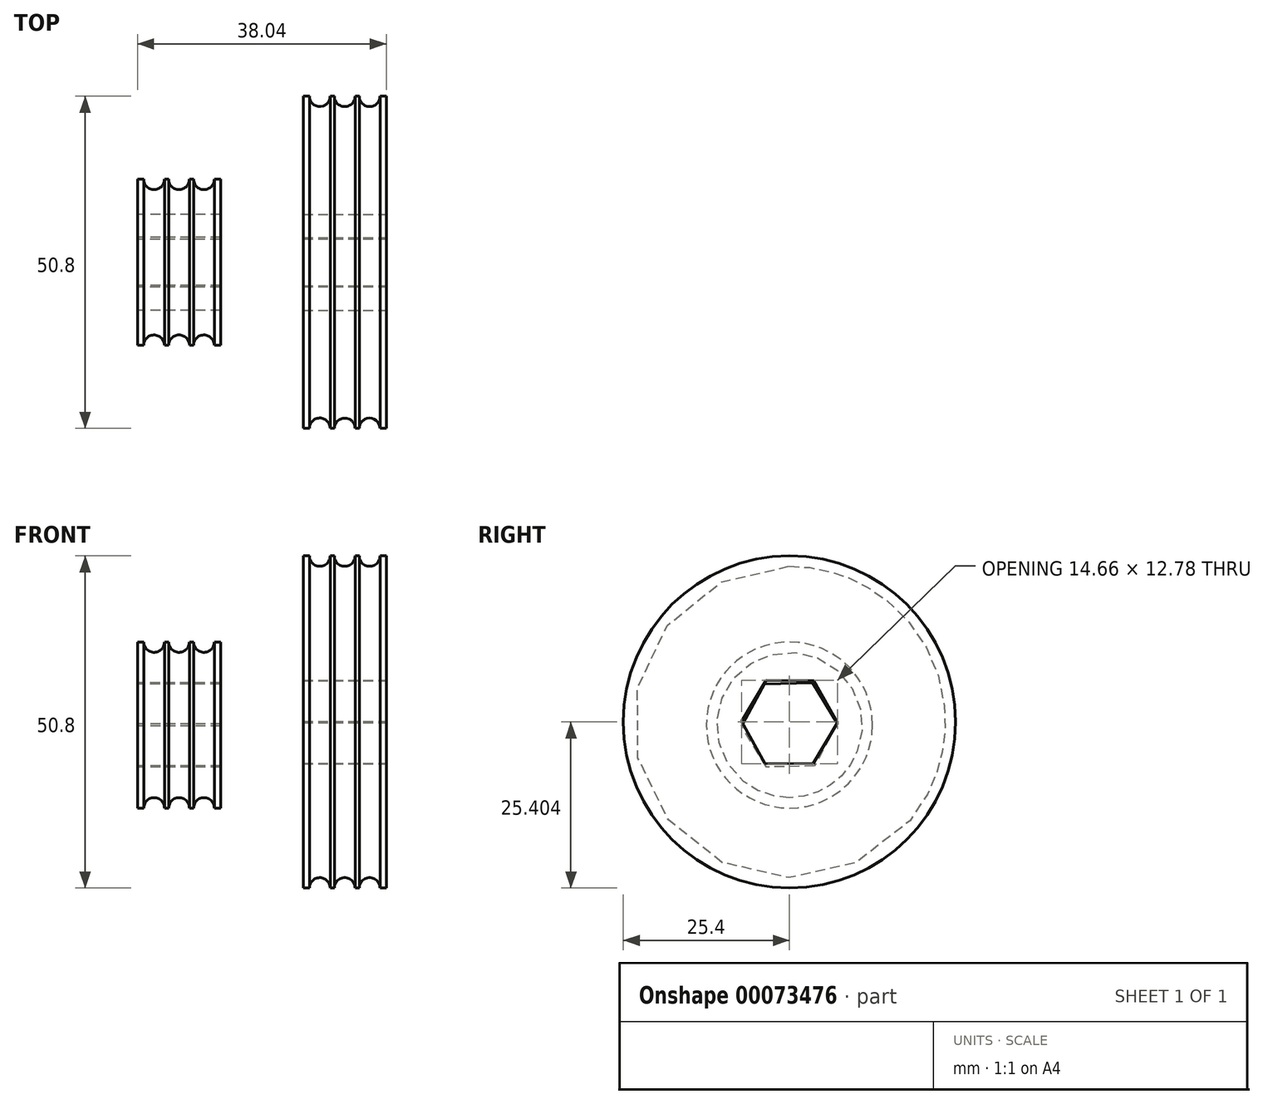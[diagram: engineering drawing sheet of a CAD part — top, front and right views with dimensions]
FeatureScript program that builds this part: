
annotation { "Feature Type Name" : "Feature", "Feature Type Description" : "" }
export const myFeature = defineFeature(function(context is Context, id is Id, definition is map)
    precondition{}
    {
        {
            var Q0;
            Q0=qCreatedBy(makeId("Front.planeOp"),FACE);
            var sketch = newSketch(context, id + "F0", { "sketchPlane" : qUnion([Q0])});
            skArc(sketch, "E0", {"start": v(1.58, 24.65) * mm, "mid": v(3.17, 23.06) * mm, "end": v(4.76, 24.65) * mm});
            skArc(sketch, "E1", {"start": v(5.4, 24.65) * mm, "mid": v(6.98, 23.06) * mm, "end": v(8.57, 24.65) * mm});
            skArc(sketch, "E2", {"start": v(9.2, 24.65) * mm, "mid": v(10.8, 23.06) * mm, "end": v(12.38, 24.65) * mm});
            skLineSegment(sketch, "E3", {"start": v(0.63, 24.65) * mm, "end": v(1.58, 24.65) * mm});
            skLineSegment(sketch, "E4", {"start": v(0.63, 11.95) * mm, "end": v(0.63, 24.65) * mm});
            skLineSegment(sketch, "E5", {"start": v(13.33, 24.65) * mm, "end": v(13.33, 11.95) * mm});
            skLineSegment(sketch, "E6.trimOffspring", {"start": v(4.76, 24.65) * mm, "end": v(5.4, 24.65) * mm});
            skLineSegment(sketch, "E7.trimOffspring", {"start": v(8.57, 24.65) * mm, "end": v(9.2, 24.65) * mm});
            skLineSegment(sketch, "E8.trimOffspring", {"start": v(12.38, 24.65) * mm, "end": v(13.33, 24.65) * mm});
            skPoint(sketch, "E9.start.orphan", {"position": v(-0.82, 11.95) * mm});
            skLineSegment(sketch, "E10", {"start": v(13.33, 11.95) * mm, "end": v(0.63, 11.95) * mm});
            skSolve(sketch);
        }
        {
            var Q0;
            Q0=makeQuery(id+"F0.imprint","IMPRINT",FACE,{"disambiguationData":[TD([[makeQuery(id+"F0.imprint","IMPRINT",EDGE,{"derivedFrom":sQuery(id+"F0.wireOp",EDGE,"E0")}),-1.0]])]});
            var Q1;
            Q1=sQuery(id+"F0.wireOp",EDGE,"E10");
            revolve(context, id + "F1", {"entities" : qUnion([Q0]), "axis" : qUnion([Q1]), "revolveType" : RevolveType.FULL});
        }
        {
            var Q0;
            Q0=qCreatedBy(makeId("Right.planeOp"),FACE);
            var sketch = newSketch(context, id + "F2", { "sketchPlane" : qUnion([Q0])});
            skCircle(sketch, "E11.cCircle", {"center": v(0, 11.95) * mm, "radius": 6.35 * mm, "construction": true});
            skLineSegment(sketch, "E11.0", {"start": v(7.33, 12.12) * mm, "end": v(3.81, 5.69) * mm});
            skLineSegment(sketch, "E11.1", {"start": v(3.81, 5.69) * mm, "end": v(-3.52, 5.52) * mm});
            skLineSegment(sketch, "E11.2", {"start": v(-3.52, 5.52) * mm, "end": v(-7.33, 11.78) * mm});
            skLineSegment(sketch, "E11.3", {"start": v(-7.33, 11.78) * mm, "end": v(-3.81, 18.21) * mm});
            skLineSegment(sketch, "E11.4", {"start": v(-3.81, 18.21) * mm, "end": v(3.52, 18.38) * mm});
            skLineSegment(sketch, "E11.5", {"start": v(3.52, 18.38) * mm, "end": v(7.33, 12.12) * mm});
            skPoint(sketch, "E11.0.midPoint", {"position": v(5.57, 8.9) * mm});
            skSolve(sketch);
        }
        {
            var Q0;
            Q0=makeQuery(id+"F2.imprint","IMPRINT",FACE,{"disambiguationData":[TD([[makeQuery(id+"F2.imprint","IMPRINT",EDGE,{"derivedFrom":sQuery(id+"F2.wireOp",EDGE,"E11.0")}),-1.0]])]});
            extrude(context, id + "F3", {"entities" : qUnion([Q0]), "operationType" : NewBodyOperationType.REMOVE, "endBound" : BoundingType.THROUGH_ALL, "depth" : 25.4 * mm});
        }
        {
            var Q0;
            Q0=qCreatedBy(makeId("Front.planeOp"),FACE);
            var sketch = newSketch(context, id + "F4", { "sketchPlane" : qUnion([Q0])});
            skArc(sketch, "E12", {"start": v(26.92, 37.81) * mm, "mid": v(28.5, 36.23) * mm, "end": v(30.1, 37.81) * mm});
            skArc(sketch, "E13", {"start": v(30.73, 37.81) * mm, "mid": v(32.32, 36.23) * mm, "end": v(33.9, 37.81) * mm});
            skArc(sketch, "E14", {"start": v(34.54, 37.81) * mm, "mid": v(36.13, 36.23) * mm, "end": v(37.71, 37.81) * mm});
            skLineSegment(sketch, "E15.bottom", {"start": v(25.97, 37.81) * mm, "end": v(26.92, 37.81) * mm});
            skLineSegment(sketch, "E15.top", {"start": v(25.97, 12.41) * mm, "end": v(38.67, 12.41) * mm});
            skLineSegment(sketch, "E15.left", {"start": v(25.97, 37.81) * mm, "end": v(25.97, 12.41) * mm});
            skLineSegment(sketch, "E15.right", {"start": v(38.67, 37.81) * mm, "end": v(38.67, 12.41) * mm});
            skLineSegment(sketch, "E16.trimOffspring", {"start": v(30.1, 37.81) * mm, "end": v(30.73, 37.81) * mm});
            skLineSegment(sketch, "E17.trimOffspring", {"start": v(33.9, 37.81) * mm, "end": v(34.54, 37.81) * mm});
            skLineSegment(sketch, "E18.trimOffspring", {"start": v(37.71, 37.81) * mm, "end": v(38.67, 37.81) * mm});
            skSolve(sketch);
        }
        {
            var Q0;
            Q0=makeQuery(id+"F4.imprint","IMPRINT",FACE,{"disambiguationData":[TD([[makeQuery(id+"F4.imprint","IMPRINT",EDGE,{"derivedFrom":sQuery(id+"F4.wireOp",EDGE,"E12")}),-1.0]])]});
            var Q1;
            Q1=sQuery(id+"F4.wireOp",EDGE,"E15.top");
            revolve(context, id + "F5", {"entities" : qUnion([Q0]), "axis" : qUnion([Q1]), "revolveType" : RevolveType.FULL});
        }
        {
            var Q0;
            Q0=makeQuery(id+"F5.opRevolve","SWEPT_FACE",FACE,{"disambiguationData":[OSD([sQuery(id+"F4.wireOp",EDGE,"E15.right")])]});
            var sketch = newSketch(context, id + "F6", { "sketchPlane" : qUnion([Q0])});
            skCircle(sketch, "E19.cCircle", {"center": v(0, 12.41) * mm, "radius": 7.33 * mm, "construction": true});
            skLineSegment(sketch, "E19.0", {"start": v(3.74, 18.72) * mm, "end": v(7.33, 12.33) * mm});
            skLineSegment(sketch, "E19.1", {"start": v(7.33, 12.33) * mm, "end": v(3.6, 6.02) * mm});
            skLineSegment(sketch, "E19.2", {"start": v(3.6, 6.02) * mm, "end": v(-3.74, 6.1) * mm});
            skLineSegment(sketch, "E19.3", {"start": v(-3.74, 6.1) * mm, "end": v(-7.33, 12.5) * mm});
            skLineSegment(sketch, "E19.4", {"start": v(-7.33, 12.5) * mm, "end": v(-3.6, 18.8) * mm});
            skLineSegment(sketch, "E19.5", {"start": v(-3.6, 18.8) * mm, "end": v(3.74, 18.72) * mm});
            skSolve(sketch);
        }
        {
            var Q0;
            Q0=makeQuery(id+"F6.imprint","IMPRINT",FACE,{"disambiguationData":[TD([[makeQuery(id+"F6.imprint","IMPRINT",EDGE,{"derivedFrom":sQuery(id+"F6.wireOp",EDGE,"E19.0")}),-1.0]])]});
            extrude(context, id + "F7", {"entities" : qUnion([Q0]), "operationType" : NewBodyOperationType.REMOVE, "oppositeDirection" : true, "depth" : 25.4 * mm});
        }
    });
